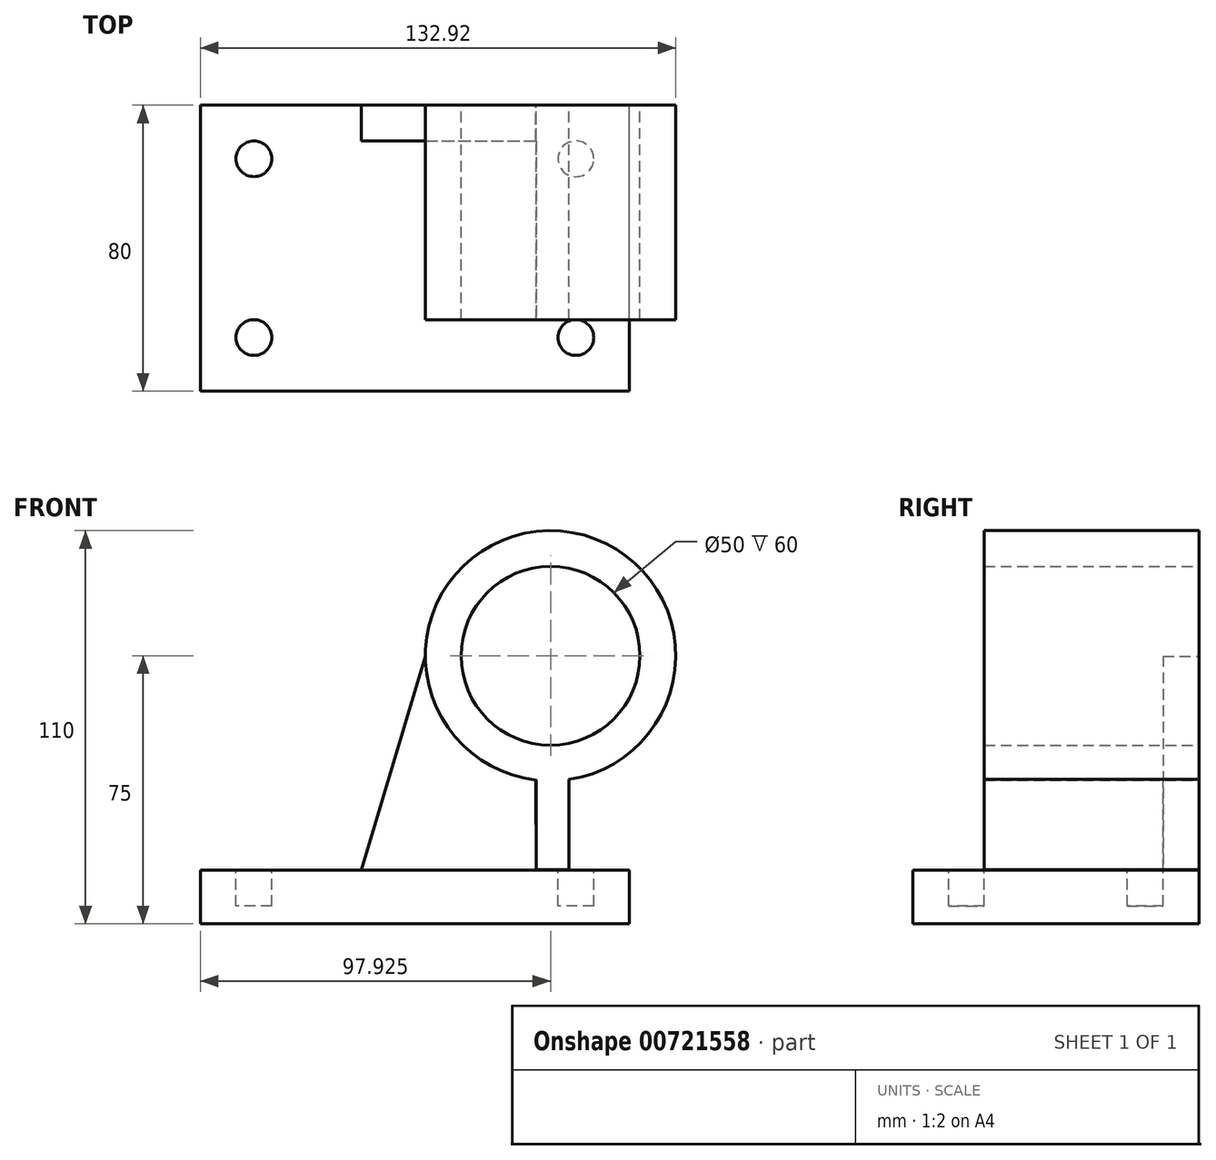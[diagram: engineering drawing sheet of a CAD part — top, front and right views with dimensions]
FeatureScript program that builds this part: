
annotation { "Feature Type Name" : "Feature", "Feature Type Description" : "" }
export const myFeature = defineFeature(function(context is Context, id is Id, definition is map)
    precondition{}
    {
        {
            var Q0;
            Q0=qCreatedBy(makeId("Front.planeOp"),FACE);
            var sketch = newSketch(context, id + "F0", { "sketchPlane" : qUnion([Q0])});
            skLineSegment(sketch, "E0.bottom", {"start": v(0, 0) * mm, "end": v(-120, 0) * mm});
            skLineSegment(sketch, "E0.top", {"start": v(0, 15) * mm, "end": v(-120, 15) * mm});
            skLineSegment(sketch, "E0.left", {"start": v(0, 0) * mm, "end": v(0, 15) * mm});
            skLineSegment(sketch, "E0.right", {"start": v(-120, 0) * mm, "end": v(-120, 15) * mm});
            skSolve(sketch);
        }
        {
            var Q0;
            Q0=makeQuery(id+"F0.imprint","IMPRINT",FACE,{"disambiguationData":[TD([[makeQuery(id+"F0.imprint","IMPRINT",EDGE,{"derivedFrom":sQuery(id+"F0.wireOp",EDGE,"E0.bottom")}),-1.0]])]});
            extrude(context, id + "F1", {"entities" : qUnion([Q0]), "depth" : 80 * mm, "offsetDistance" : 25 * mm});
        }
        {
            var Q0;
            Q0=makeQuery(id+"F1.opExtrude","SWEPT_FACE",FACE,{"disambiguationData":[OSD([sQuery(id+"F0.wireOp",EDGE,"E0.top")])]});
            var sketch = newSketch(context, id + "F2", { "sketchPlane" : qUnion([Q0])});
            skCircle(sketch, "E1", {"center": v(-105, -15) * mm, "radius": 5 * mm});
            skCircle(sketch, "E2", {"center": v(-105, -65) * mm, "radius": 5 * mm});
            skCircle(sketch, "E3", {"center": v(-15, -65) * mm, "radius": 5 * mm});
            skCircle(sketch, "E4", {"center": v(-15, -15) * mm, "radius": 5 * mm});
            skSolve(sketch);
        }
        {
            var Q0;
            Q0=makeQuery(id+"F2.imprint","IMPRINT",FACE,{"disambiguationData":[TD([[makeQuery(id+"F2.imprint","IMPRINT",EDGE,{"derivedFrom":sQuery(id+"F2.wireOp",EDGE,"E1")}),1.0]])]});
            var Q1;
            Q1=makeQuery(id+"F2.imprint","IMPRINT",FACE,{"disambiguationData":[TD([[makeQuery(id+"F2.imprint","IMPRINT",EDGE,{"derivedFrom":sQuery(id+"F2.wireOp",EDGE,"E4")}),1.0]])]});
            var Q2;
            Q2=makeQuery(id+"F2.imprint","IMPRINT",FACE,{"disambiguationData":[TD([[makeQuery(id+"F2.imprint","IMPRINT",EDGE,{"derivedFrom":sQuery(id+"F2.wireOp",EDGE,"E2")}),1.0]])]});
            var Q3;
            Q3=makeQuery(id+"F2.imprint","IMPRINT",FACE,{"disambiguationData":[TD([[makeQuery(id+"F2.imprint","IMPRINT",EDGE,{"derivedFrom":sQuery(id+"F2.wireOp",EDGE,"E3")}),1.0]])]});
            extrude(context, id + "F3", {"entities" : qUnion([Q0, Q1, Q2, Q3]), "operationType" : NewBodyOperationType.REMOVE, "oppositeDirection" : true, "depth" : 10 * mm, "offsetDistance" : 25 * mm});
        }
        {
            var Q0;
            Q0=qCreatedBy(makeId("Front.planeOp"),FACE);
            var sketch = newSketch(context, id + "F4", { "sketchPlane" : qUnion([Q0])});
            skCircle(sketch, "E5", {"center": v(-22.08, 75) * mm, "radius": 35 * mm});
            skCircle(sketch, "E6", {"center": v(-22.08, 75) * mm, "radius": 25 * mm});
            skPoint(sketch, "E7.end.orphan", {"position": v(-27.32, 33.03) * mm});
            skPoint(sketch, "E7.start.orphan", {"position": v(-22.57, 33.03) * mm});
            skPoint(sketch, "E8.start.orphan", {"position": v(-32.57, 33.03) * mm});
            skLineSegment(sketch, "E9.top", {"start": v(-26.14, 15.17) * mm, "end": v(-16.92, 15.17) * mm});
            skLineSegment(sketch, "E9.left", {"start": v(-26.14, 40.24) * mm, "end": v(-26.14, 15.17) * mm});
            skLineSegment(sketch, "E9.right", {"start": v(-16.92, 40.38) * mm, "end": v(-16.92, 15.17) * mm});
            skSolve(sketch);
        }
        {
            var Q0;
            Q0=makeQuery(id+"F4.imprint","IMPRINT",FACE,{"disambiguationData":[TD([[makeQuery(id+"F4.imprint","IMPRINT",EDGE,{"derivedFrom":sQuery(id+"F4.wireOp",EDGE,"E6")}),-1.0]])]});
            var Q1;
            Q1=makeQuery(id+"F4.imprint","IMPRINT",FACE,{"disambiguationData":[TD([[makeQuery(id+"F4.imprint","IMPRINT",EDGE,{"derivedFrom":sQuery(id+"F4.wireOp",EDGE,"E9.top")}),1.0]])]});
            extrude(context, id + "F5", {"entities" : qUnion([Q0, Q1]), "depth" : 60 * mm, "offsetDistance" : 25 * mm});
        }
        {
            var Q0;
            Q0=qCreatedBy(makeId("Front.planeOp"),FACE);
            var sketch = newSketch(context, id + "F6", { "sketchPlane" : qUnion([Q0])});
            skLineSegment(sketch, "E10", {"start": v(-57.05, 75) * mm, "end": v(-75, 15.02) * mm});
            skLineSegment(sketch, "E11", {"start": v(-75, 15.02) * mm, "end": v(-26.14, 15.17) * mm});
            skLineSegment(sketch, "E12", {"start": v(-26.14, 15.17) * mm, "end": v(-26.22, 40.25) * mm});
            skArc(sketch, "E13", {"start": v(-57.05, 75) * mm, "mid": v(-48.2, 51.8) * mm, "end": v(-26.22, 40.25) * mm});
            skSolve(sketch);
        }
        {
            var Q0;
            Q0=makeQuery(id+"F6.imprint","IMPRINT",FACE,{"disambiguationData":[TD([[makeQuery(id+"F6.imprint","IMPRINT",EDGE,{"derivedFrom":sQuery(id+"F6.wireOp",EDGE,"E10")}),1.0]])]});
            extrude(context, id + "F7", {"entities" : qUnion([Q0]), "operationType" : NewBodyOperationType.ADD, "depth" : 10 * mm, "offsetDistance" : 25 * mm});
        }
    });
